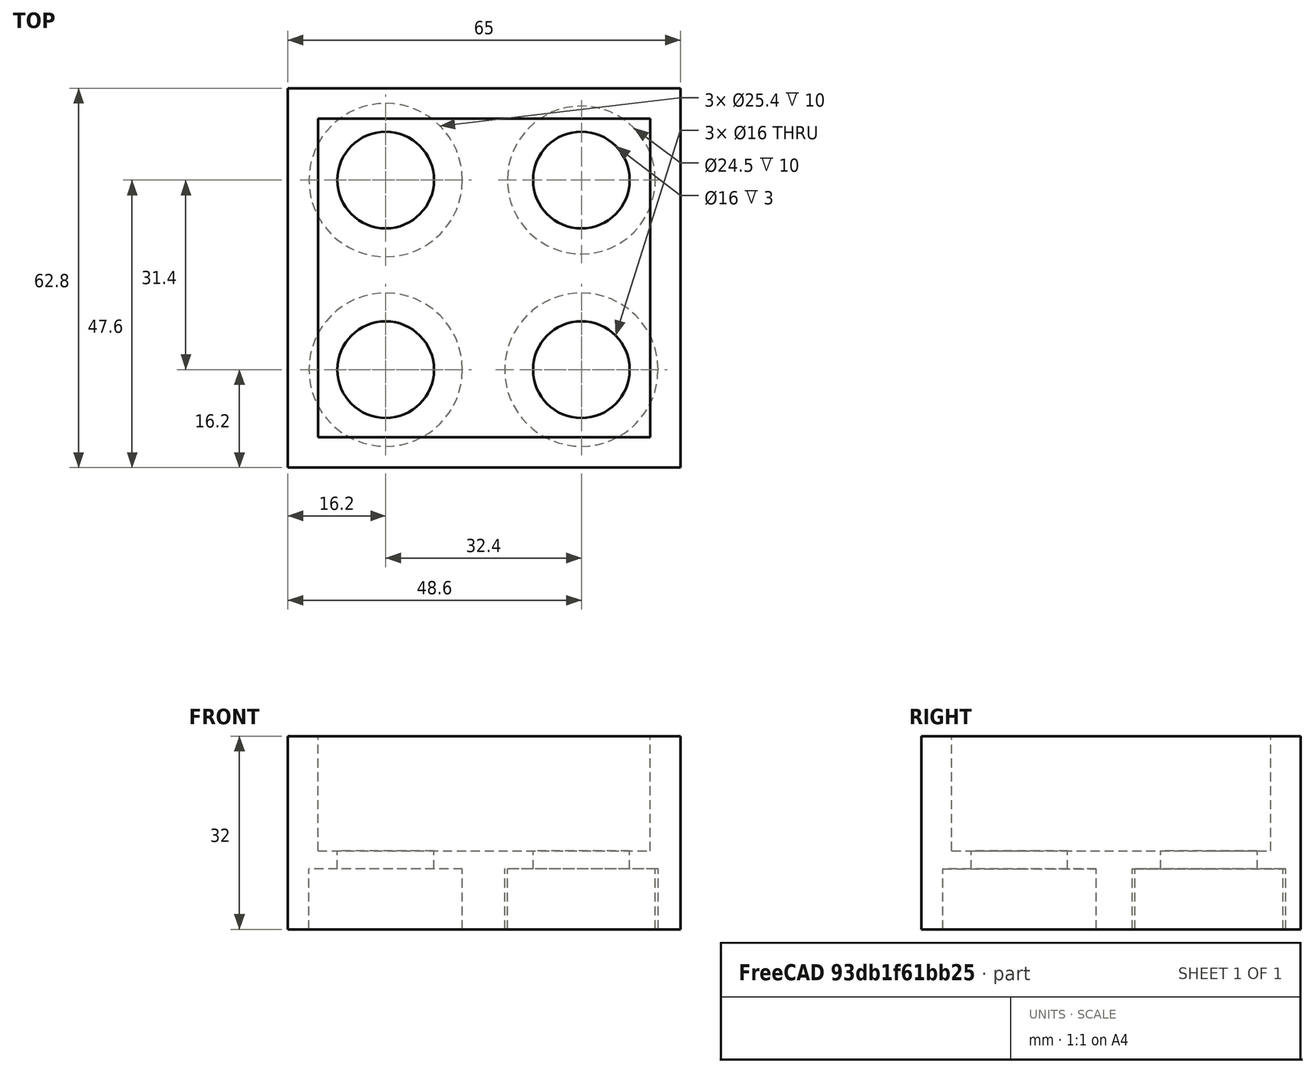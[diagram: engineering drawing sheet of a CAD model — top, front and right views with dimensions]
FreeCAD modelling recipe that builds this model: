
FCSTD DOCUMENT  (FreeCAD 0.18R16110 (Git))
Label: vial-25-rack
License: All rights reserved
LicenseURL: http://en.wikipedia.org/wiki/All_rights_reserved
objects: Part::Cut×9, Part::Cylinder×8, Part::Box×3, Part::Fuse×1, Mesh::Feature×1
note: 21 computed .brp shape members not serialized (recipe doc carries the construction recipe); baked Part::Feature solids carry a one-line shape summary decoded from their .brp

FEATURE [Part::Cylinder] Cylinder001  label="Zylinder001"
  Angle = 360
  AttacherType = Attacher::AttachEngine3D
  Height = 10
  Placement = pos=(32.4,0,0) rot=(0,0,1;0rad)
  Radius = 12.7
  expr: Placement.Base.x = 22.4 + 10
  expr: Radius = 25.4 / 2
FEATURE [Part::Cylinder] Cylinder004  label="Zylinder004"
  Angle = 360
  AttacherType = Attacher::AttachEngine3D
  Height = 10
  Placement = pos=(0,31.4,0) rot=(0,0,1;0rad)
  Radius = 12.7
  expr: Placement.Base.y = 22.4 / 2 + 20.4 / 2 + 10
  expr: Radius = 25.4 / 2
FEATURE [Part::Cylinder] Cylinder006  label="Zylinder006"
  Angle = 360
  AttacherType = Attacher::AttachEngine3D
  Height = 10
  Placement = pos=(32.4,31.4,0) rot=(0,0,1;0rad)
  Radius = 12.25
  expr: Placement.Base.x = 22.4 + 10
  expr: Placement.Base.y = 22.4 / 2 + 20.4 / 2 + 10
  expr: Radius = 24.5 / 2
FEATURE [Part::Box] Box  label="Quader"
  AttacherType = Attacher::AttachEngine3D
  Height = 13
  Length = 65
  Placement = pos=(-16.2,-16.2,0) rot=(0,0,1;0rad)
  Width = 62.8
  expr: Length = 65
  expr: Placement.Base.y = -22.4 / 2 - 5
  expr: Placement.Base.x = -22.4 / 2 - 5
FEATURE [Part::Box] Box001  label="Quader001"
  AttacherType = Attacher::AttachEngine3D
  Height = 19
  Length = 65
  Placement = pos=(-16.2,-16.2,13) rot=(0,0,1;0rad)
  Width = 62.8
  expr: Placement.Base.y = -22.4 / 2 - 5
  expr: Placement.Base.x = -22.4 / 2 - 5
FEATURE [Part::Box] Box002  label="Quader002"
  AttacherType = Attacher::AttachEngine3D
  Height = 19
  Length = 55
  Placement = pos=(-11.2,-11.2,13) rot=(0,0,1;0rad)
  Width = 52.8
  expr: Placement.Base.y = -22.4 / 2
  expr: Placement.Base.x = -22.4 / 2
FEATURE [Part::Cylinder] Cylinder008  label="Zylinder008"
  Angle = 360
  AttacherType = Attacher::AttachEngine3D
  Height = 18
  Radius = 8
FEATURE [Part::Cylinder] Cylinder009  label="Zylinder009"
  Angle = 360
  AttacherType = Attacher::AttachEngine3D
  Height = 18
  Placement = pos=(32.4,0,0) rot=(0,0,1;0rad)
  Radius = 8
  expr: Placement.Base.x = 32.4
FEATURE [Part::Cylinder] Cylinder014  label="Zylinder014"
  Angle = 360
  AttacherType = Attacher::AttachEngine3D
  Height = 18
  Placement = pos=(32.4,31.4,0) rot=(0,0,1;0rad)
  Radius = 8
  expr: Placement.Base.x = 32.4
FEATURE [Part::Cylinder] Cylinder015  label="Zylinder015"
  Angle = 360
  AttacherType = Attacher::AttachEngine3D
  Height = 18
  Placement = pos=(0,31.4,0) rot=(0,0,1;0rad)
  Radius = 8
FEATURE [Part::Cylinder] Cylinder  label="Zylinder"
  Angle = 360
  AttacherType = Attacher::AttachEngine3D
  Height = 10
  Radius = 12.7
  expr: Radius = 25.4 / 2
FEATURE [Part::Cut] Cut
  Base = -> Box
  Tool = -> Cylinder006
FEATURE [Part::Cut] Cut009
  Base = -> Cut
  Tool = -> Cylinder004
FEATURE [Part::Cut] Cut010
  Base = -> Cut009
  Tool = -> Cylinder
FEATURE [Part::Cut] Cut011
  Base = -> Cut010
  Tool = -> Cylinder001
FEATURE [Part::Cut] Cut012
  Base = -> Box001
  Tool = -> Box002
FEATURE [Part::Fuse] Fusion
  Base = -> Cut011
  Tool = -> Cut012
FEATURE [Part::Cut] Cut013
  Base = -> Fusion
  Tool = -> Cylinder008
FEATURE [Part::Cut] Cut014
  Base = -> Cut013
  Tool = -> Cylinder014
FEATURE [Part::Cut] Cut015
  Base = -> Cut014
  Tool = -> Cylinder015
FEATURE [Part::Cut] Cut016  label="vial-25-rack"
  Base = -> Cut015
  Tool = -> Cylinder009
FEATURE [Mesh::Feature] Mesh001  label="vial-25-rack(Meshed)"
